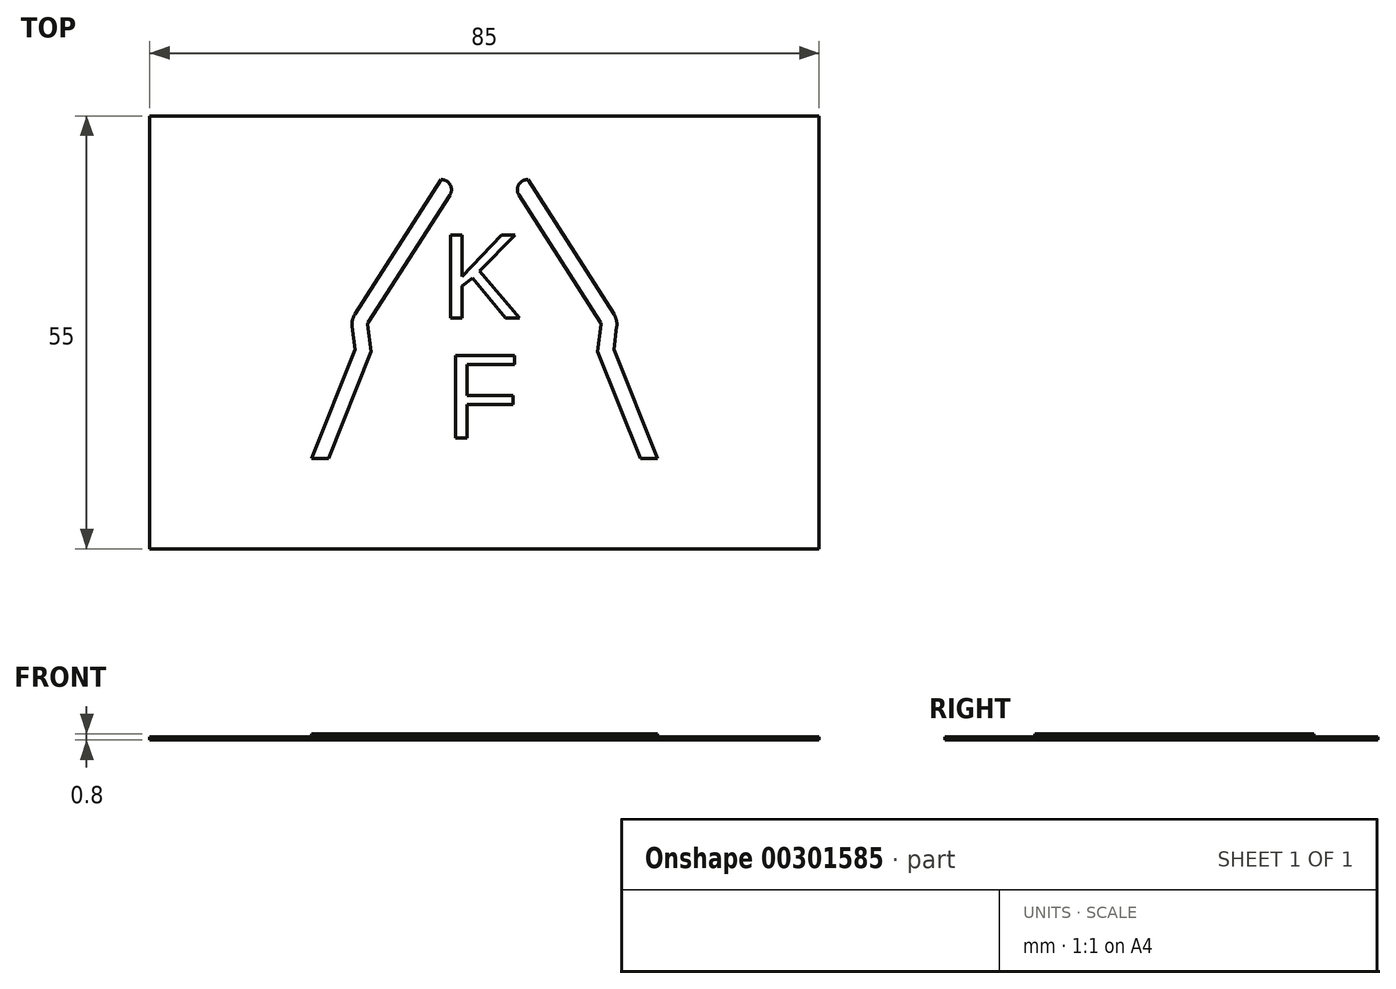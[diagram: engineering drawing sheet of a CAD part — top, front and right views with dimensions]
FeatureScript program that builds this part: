
annotation { "Feature Type Name" : "Feature", "Feature Type Description" : "" }
export const myFeature = defineFeature(function(context is Context, id is Id, definition is map)
    precondition{}
    {
        {
            var Q0;
            Q0=qCreatedBy(makeId("Top.planeOp"),FACE);
            var sketch = newSketch(context, id + "F0", { "sketchPlane" : qUnion([Q0])});
            skLineSegment(sketch, "E0.bottom", {"start": v(-42.5, 27.5) * mm, "end": v(42.5, 27.5) * mm});
            skLineSegment(sketch, "E0.top", {"start": v(-42.5, -27.5) * mm, "end": v(42.5, -27.5) * mm});
            skLineSegment(sketch, "E0.left", {"start": v(-42.5, 27.5) * mm, "end": v(-42.5, -27.5) * mm});
            skLineSegment(sketch, "E0.right", {"start": v(42.5, 27.5) * mm, "end": v(42.5, -27.5) * mm});
            skSolve(sketch);
        }
        {
            var Q0;
            Q0 = qSketchRegion(id + "F0", true);
            extrude(context, id + "F1", {"entities" : qUnion([Q0]), "depth" : 0.4 * mm});
        }
        {
            var Q0;
            Q0=makeQuery(id+"F1.opExtrude","CAP_FACE",FACE,{"disambiguationData":[OSD([sQuery(id+"F0.wireOp",EDGE,"E0.bottom"),sQuery(id+"F0.wireOp",EDGE,"E0.top"),sQuery(id+"F0.wireOp",EDGE,"E0.left"),sQuery(id+"F0.wireOp",EDGE,"E0.right")])],"isStart":false});
            var sketch = newSketch(context, id + "F2", { "sketchPlane" : qUnion([Q0])});
            skLineSegment(sketch, "E1", {"start": v(-5.53, 19.38) * mm, "end": v(-16.46, 2.3) * mm});
            skArc(sketch, "E2", {"start": v(-16.46, 2.3) * mm, "mid": v(-16.77, 1.54) * mm, "end": v(-16.81, 0.72) * mm});
            skLineSegment(sketch, "E3", {"start": v(-16.81, 0.72) * mm, "end": v(-16.45, -2.18) * mm});
            skLineSegment(sketch, "E4", {"start": v(-16.45, -2.18) * mm, "end": v(-21.97, -16.04) * mm});
            skLineSegment(sketch, "E5", {"start": v(-21.97, -16.04) * mm, "end": v(-19.81, -16.04) * mm});
            skLineSegment(sketch, "E6.0", {"start": v(-14.4, -2.44) * mm, "end": v(-19.81, -16.04) * mm});
            skLineSegment(sketch, "E6.1", {"start": v(-14.83, 0.97) * mm, "end": v(-14.4, -2.44) * mm});
            skArc(sketch, "E6.2", {"start": v(-14.77, 1.21) * mm, "mid": v(-14.82, 1.1) * mm, "end": v(-14.83, 0.97) * mm});
            skLineSegment(sketch, "E6.3", {"start": v(-4.39, 17.46) * mm, "end": v(-14.77, 1.21) * mm});
            skArc(sketch, "E7", {"start": v(-4.39, 17.46) * mm, "mid": v(-4.36, 18.77) * mm, "end": v(-5.53, 19.38) * mm});
            skArc(sketch, "E8.MirrorCS", {"start": v(14.77, 1.21) * mm, "mid": v(14.82, 1.1) * mm, "end": v(14.83, 0.97) * mm});
            skLineSegment(sketch, "E9.MirrorCS", {"start": v(21.97, -16.04) * mm, "end": v(19.81, -16.04) * mm});
            skArc(sketch, "E10.MirrorCS", {"start": v(16.46, 2.3) * mm, "mid": v(16.77, 1.54) * mm, "end": v(16.81, 0.72) * mm});
            skArc(sketch, "E11.MirrorCS", {"start": v(4.39, 17.46) * mm, "mid": v(4.36, 18.77) * mm, "end": v(5.53, 19.38) * mm});
            skLineSegment(sketch, "E12.MirrorCS", {"start": v(4.39, 17.46) * mm, "end": v(14.77, 1.21) * mm});
            skLineSegment(sketch, "E13.MirrorCS", {"start": v(14.4, -2.44) * mm, "end": v(19.81, -16.04) * mm});
            skLineSegment(sketch, "E14.MirrorCS", {"start": v(16.45, -2.18) * mm, "end": v(21.97, -16.04) * mm});
            skLineSegment(sketch, "E15.MirrorCS", {"start": v(16.81, 0.72) * mm, "end": v(16.45, -2.18) * mm});
            skLineSegment(sketch, "E16.MirrorCS", {"start": v(5.53, 19.38) * mm, "end": v(16.46, 2.3) * mm});
            skLineSegment(sketch, "E17.MirrorCS", {"start": v(14.83, 0.97) * mm, "end": v(14.4, -2.44) * mm});
            skText(sketch, "E18", { "text": "K", "fontName": "Arimo-Regular.ttf"});
            skText(sketch, "E19", { "text": "F", "fontName": "Arimo-Regular.ttf"});
            const initialGuessF2  = {"E18": [-0.00554, 0.00184, 1, 0, 0.011], "E19": [-0.0049, -0.01344, 1, 0, 0.011]};
            skSetInitialGuess(sketch, initialGuessF2);
            skSolve(sketch);
        }
        {
            var Q0;
            Q0 = qSketchRegion(id + "F2", true);
            extrude(context, id + "F3", {"entities" : qUnion([Q0]), "operationType" : NewBodyOperationType.ADD, "depth" : 0.4 * mm});
        }
    });
